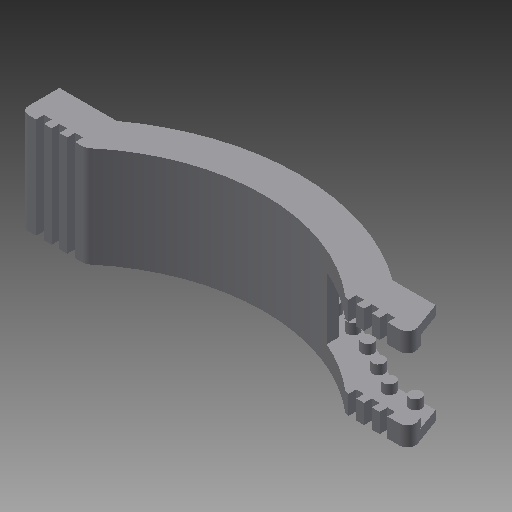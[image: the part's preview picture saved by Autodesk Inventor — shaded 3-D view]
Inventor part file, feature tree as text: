
AUTODESK INVENTOR PART (.ipt)
format: ipt  version: 2018 (Build 220112000, 112)  size: 281,600 bytes
history: native  units: in
note: dims shown in document units (in); Inventor stores cm internally (conversion verified against a paired STEP export)
features: reference x29, plane x6, sketch x6, extrude x6, pattern_linear x2, mirror x1, fillet x1
ambient origin geometry x8: Origin, YZ Plane, XZ Plane, XY Plane, X Axis, Y Axis, Z Axis, Center Point
bodies: Solid1 (feature_tree)
feature tree (51):
  plane  "Work Plane2"
  sketch  "Sketch3"  dims[d4=0.0625in d5=0.0in d6=0.125in d7=0.0in]
  plane  "Work Plane3"
  extrude  "Extrusion1"  Depth=0.125in TaperAngle=0.0deg
  sketch  "Sketch4"  dims[d8=0.25in d9=0.0in d10=0.0in]
  plane  "Work Plane4"
  extrude  "Extrusion2"  TaperAngle=0.0deg  [1 undecoded]
  plane  "Work Plane5"
  mirror  "Mirror1"
  extrude  "Extrusion3"  Depth=0.05in
  sketch  "Sketch7"  dims[d15=0.1in d16=0.05in d17=0.3125in d18=0.0in]
  plane  "Work Plane6"
  plane  "Work Plane7"
  extrude  "Extrusion7"  Depth=0.05in
  fillet  "Fillet1"  Radius=0.3125in
  extrude  "Extrusion5"  Depth=0.05in
  pattern_linear  "Rectangular Pattern1"  Count1=3 Spacing1=0.1in
  extrude  "Extrusion6"  Depth=0.05in
  pattern_linear  "Rectangular Pattern2"  Spacing1=0.4375in  [1 undecoded]
  reference  "Reference10"
  reference  "Reference11"
  reference  "Reference12"
  reference  "Reference13"
  reference  "Reference14"
  reference  "Reference15"
  reference  "Reference16"
  reference  "Reference17"
  reference  "Reference18"
  reference  "Reference19"
  reference  "Reference20"
  reference  "Reference21"
  reference  "Reference22"
  reference  "Reference23"
  reference  "Reference24"
  reference  "Reference25"
  reference  "Reference26"
  reference  "Reference27"
  reference  "Reference28"
  reference  "Reference29"
  reference  "Reference30"
  reference  "Reference31"
  reference  "Reference32"
  reference  "Reference33"
  sketch  "Sketch6"  dims[d13=0.05in d14=0.05in]
  reference  "Reference34"
  reference  "Reference35"
  reference  "Reference36"
  reference  "Reference37"
  reference  "Reference38"
  sketch  "Sketch8"  dims[d19=1.1811in d21=0.1in d22=0.05in]
  sketch  "Sketch9"  dims[d23=0.75in d24=0.0in d25=1.1811in d27=0.1in d28=0.05in d29=0.4375in d30=0.0in]
note: 2 required parameter values undecoded (feature->parameter linkage not recoverable at this tier; creation-order binding heuristic only, values carry confidence <= 0.55)
